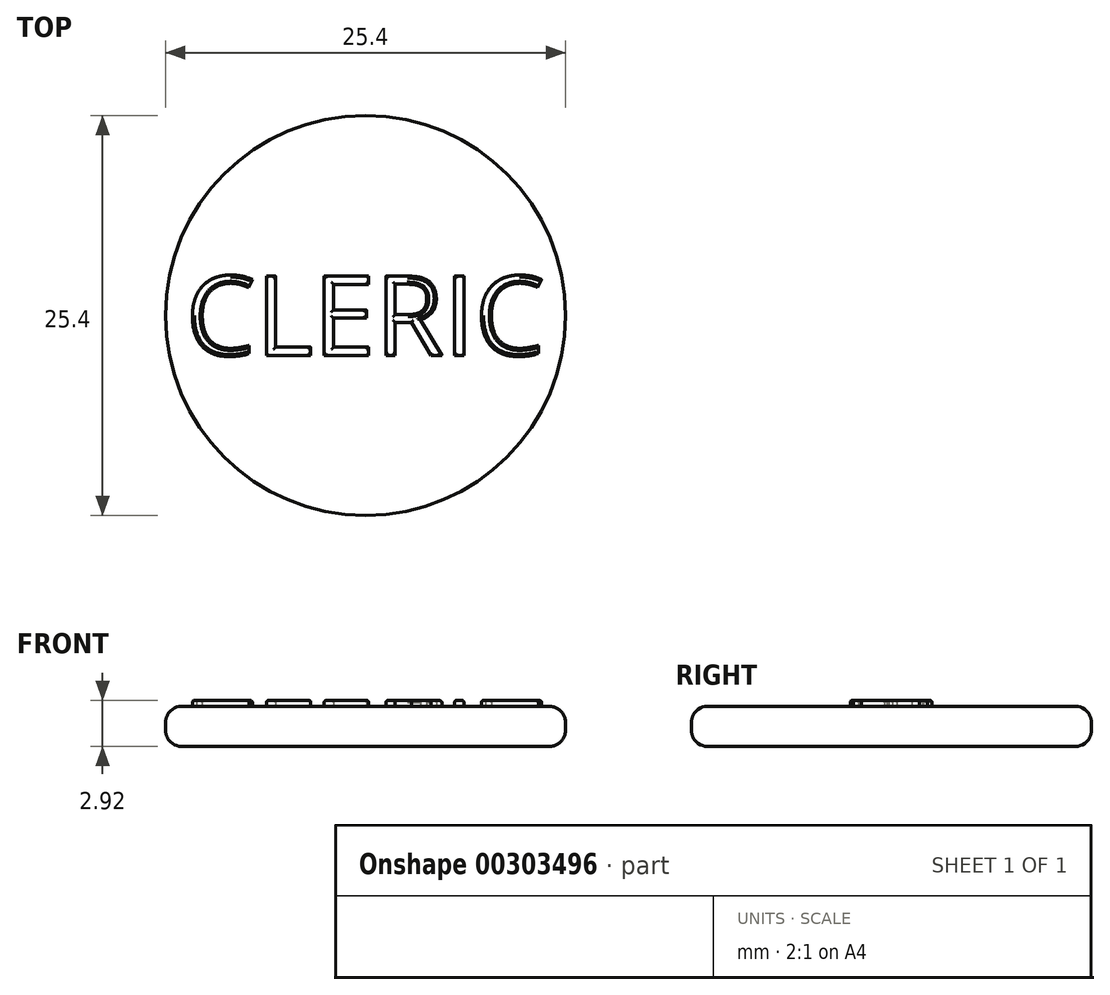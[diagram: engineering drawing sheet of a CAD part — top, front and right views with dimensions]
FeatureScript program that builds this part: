
annotation { "Feature Type Name" : "Feature", "Feature Type Description" : "" }
export const myFeature = defineFeature(function(context is Context, id is Id, definition is map)
    precondition{}
    {
        {
            var Q0;
            Q0=qCreatedBy(makeId("Top.planeOp"),FACE);
            var sketch = newSketch(context, id + "F0", { "sketchPlane" : qUnion([Q0])});
            skCircle(sketch, "E0", {"center": v(0, 0) * mm, "radius": 12.7 * mm});
            skLineSegment(sketch, "E1", {"start": v(0, 0) * mm, "end": v(-11.43, 0) * mm});
            skLineSegment(sketch, "E2", {"start": v(-11.43, 0) * mm, "end": v(-11.43, 2.54) * mm});
            skLineSegment(sketch, "E3", {"start": v(-11.43, 0) * mm, "end": v(-11.43, -2.54) * mm});
            skText(sketch, "E4", { "text": "CLERIC", "fontName": "OpenSans-Regular.ttf"});
            const initialGuessF0  = {"E4": [-0.01143, -0.00254, 1, 0, 0.00508]};
            skSetInitialGuess(sketch, initialGuessF0);
            skSolve(sketch);
        }
        {
            var Q0;
            Q0 = qSketchRegion(id + "F0", true);
            var Q1;
            Q1=makeQuery(id+"F0.imprint","IMPRINT",FACE,{"disambiguationData":[TD([[makeQuery(id+"F0.imprint","IMPRINT",EDGE,{"derivedFrom":sQuery(id+"F0.wireOp",EDGE,"E4.sketch_text.stroke-44")}),1.0]])]});
            extrude(context, id + "F1", {"entities" : qUnion([Q0, Q1]), "depth" : 2.54 * mm});
        }
        {
            var Q0;
            Q0=makeQuery(id+"F0.imprint","IMPRINT",FACE,{"disambiguationData":[TD([[makeQuery(id+"F0.imprint","IMPRINT",EDGE,{"derivedFrom":sQuery(id+"F0.wireOp",EDGE,"E4.sketch_text.stroke-55")}),-1.0]])]});
            var Q1;
            Q1=makeQuery(id+"F0.imprint","IMPRINT",FACE,{"disambiguationData":[TD([[makeQuery(id+"F0.imprint","IMPRINT",EDGE,{"derivedFrom":sQuery(id+"F0.wireOp",EDGE,"E4.sketch_text.stroke-51")}),-1.0]])]});
            var Q2;
            Q2=makeQuery(id+"F0.imprint","IMPRINT",FACE,{"disambiguationData":[TD([[makeQuery(id+"F0.imprint","IMPRINT",EDGE,{"derivedFrom":sQuery(id+"F0.wireOp",EDGE,"E4.sketch_text.stroke-33")}),-1.0]])]});
            var Q3;
            {var subQ0=sQuery(id+"F0.wireOp",EDGE,"E4.sketch_text.stroke-21");Q3=makeQuery(id+"F0.imprint","IMPRINT",FACE,{"disambiguationData":[TD([[makeQuery(id+"F0.imprint","IMPRINT",EDGE,{"derivedFrom":subQ0}),-1.0]])]});}
            var Q4;
            {var subQ0=sQuery(id+"F0.wireOp",EDGE,"E4.sketch_text.stroke-18");Q4=makeQuery(id+"F0.imprint","IMPRINT",FACE,{"disambiguationData":[TD([[makeQuery(id+"F0.imprint","IMPRINT",EDGE,{"derivedFrom":subQ0}),-1.0]])]});}
            var Q5;
            {var subQ5=sQuery(id+"F0.wireOp",EDGE,"E4.sketch_text.stroke-16");Q5=makeQuery(id+"F0.imprint","IMPRINT",FACE,{"disambiguationData":[TD([[makeQuery(id+"F0.imprint","IMPRINT",EDGE,{"derivedFrom":subQ5}),-1.0]])]});}
            var Q6;
            {var subQ0=sQuery(id+"F0.wireOp",EDGE,"E4.sketch_text.stroke-2");Q6=makeQuery(id+"F0.imprint","IMPRINT",FACE,{"disambiguationData":[TD([[makeQuery(id+"F0.imprint","IMPRINT",EDGE,{"derivedFrom":subQ0}),-1.0]])]});}
            var Q7;
            {var subQ4=sQuery(id+"F0.wireOp",EDGE,"E4.sketch_text.stroke-0");Q7=makeQuery(id+"F0.imprint","IMPRINT",FACE,{"disambiguationData":[TD([[makeQuery(id+"F0.imprint","IMPRINT",EDGE,{"derivedFrom":subQ4}),-1.0]])]});}
            extrude(context, id + "F2", {"entities" : qUnion([Q0, Q1, Q2, Q3, Q4, Q5, Q6, Q7]), "depth" : 2.92 * mm, "hasSecondDirection" : true, "secondDirectionOppositeDirection" : false, "secondDirectionDepth" : 0.64 * mm});
        }
        {
            var Q0;
            Q0=makeQuery(id+"F2.opExtrude","CAP_FACE",FACE,{"disambiguationData":[OSD([sQuery(id+"F0.wireOp",EDGE,"E4.sketch_text.stroke-0"),sQuery(id+"F0.wireOp",EDGE,"E4.sketch_text.stroke-1"),sQuery(id+"F0.wireOp",EDGE,"E4.sketch_text.stroke-2"),sQuery(id+"F0.wireOp",EDGE,"E4.sketch_text.stroke-3"),sQuery(id+"F0.wireOp",EDGE,"E4.sketch_text.stroke-4"),sQuery(id+"F0.wireOp",EDGE,"E4.sketch_text.stroke-5"),sQuery(id+"F0.wireOp",EDGE,"E4.sketch_text.stroke-6"),sQuery(id+"F0.wireOp",EDGE,"E4.sketch_text.stroke-7"),sQuery(id+"F0.wireOp",EDGE,"E4.sketch_text.stroke-8"),sQuery(id+"F0.wireOp",EDGE,"E4.sketch_text.stroke-9"),sQuery(id+"F0.wireOp",EDGE,"E4.sketch_text.stroke-10"),sQuery(id+"F0.wireOp",EDGE,"E4.sketch_text.stroke-11"),sQuery(id+"F0.wireOp",EDGE,"E4.sketch_text.stroke-12"),sQuery(id+"F0.wireOp",EDGE,"E4.sketch_text.stroke-13"),sQuery(id+"F0.wireOp",EDGE,"E4.sketch_text.stroke-14")])],"isStart":false});
            var Q1;
            Q1=makeQuery(id+"F2.opExtrude","CAP_FACE",FACE,{"disambiguationData":[OSD([sQuery(id+"F0.wireOp",EDGE,"E4.sketch_text.stroke-15"),sQuery(id+"F0.wireOp",EDGE,"E4.sketch_text.stroke-16"),sQuery(id+"F0.wireOp",EDGE,"E4.sketch_text.stroke-17"),sQuery(id+"F0.wireOp",EDGE,"E4.sketch_text.stroke-18"),sQuery(id+"F0.wireOp",EDGE,"E4.sketch_text.stroke-19"),sQuery(id+"F0.wireOp",EDGE,"E4.sketch_text.stroke-20")])],"isStart":false});
            var Q2;
            Q2=makeQuery(id+"F2.opExtrude","CAP_FACE",FACE,{"disambiguationData":[OSD([sQuery(id+"F0.wireOp",EDGE,"E4.sketch_text.stroke-21"),sQuery(id+"F0.wireOp",EDGE,"E4.sketch_text.stroke-22"),sQuery(id+"F0.wireOp",EDGE,"E4.sketch_text.stroke-23"),sQuery(id+"F0.wireOp",EDGE,"E4.sketch_text.stroke-24"),sQuery(id+"F0.wireOp",EDGE,"E4.sketch_text.stroke-25"),sQuery(id+"F0.wireOp",EDGE,"E4.sketch_text.stroke-26"),sQuery(id+"F0.wireOp",EDGE,"E4.sketch_text.stroke-27"),sQuery(id+"F0.wireOp",EDGE,"E4.sketch_text.stroke-28"),sQuery(id+"F0.wireOp",EDGE,"E4.sketch_text.stroke-29"),sQuery(id+"F0.wireOp",EDGE,"E4.sketch_text.stroke-30"),sQuery(id+"F0.wireOp",EDGE,"E4.sketch_text.stroke-31"),sQuery(id+"F0.wireOp",EDGE,"E4.sketch_text.stroke-32")])],"isStart":false});
            var Q3;
            Q3=makeQuery(id+"F2.opExtrude","CAP_FACE",FACE,{"disambiguationData":[OSD([sQuery(id+"F0.wireOp",EDGE,"E4.sketch_text.stroke-33"),sQuery(id+"F0.wireOp",EDGE,"E4.sketch_text.stroke-34"),sQuery(id+"F0.wireOp",EDGE,"E4.sketch_text.stroke-35"),sQuery(id+"F0.wireOp",EDGE,"E4.sketch_text.stroke-36"),sQuery(id+"F0.wireOp",EDGE,"E4.sketch_text.stroke-37"),sQuery(id+"F0.wireOp",EDGE,"E4.sketch_text.stroke-38"),sQuery(id+"F0.wireOp",EDGE,"E4.sketch_text.stroke-39"),sQuery(id+"F0.wireOp",EDGE,"E4.sketch_text.stroke-40"),sQuery(id+"F0.wireOp",EDGE,"E4.sketch_text.stroke-41"),sQuery(id+"F0.wireOp",EDGE,"E4.sketch_text.stroke-42"),sQuery(id+"F0.wireOp",EDGE,"E4.sketch_text.stroke-43"),sQuery(id+"F0.wireOp",EDGE,"E4.sketch_text.stroke-44"),sQuery(id+"F0.wireOp",EDGE,"E4.sketch_text.stroke-45"),sQuery(id+"F0.wireOp",EDGE,"E4.sketch_text.stroke-46"),sQuery(id+"F0.wireOp",EDGE,"E4.sketch_text.stroke-47"),sQuery(id+"F0.wireOp",EDGE,"E4.sketch_text.stroke-48"),sQuery(id+"F0.wireOp",EDGE,"E4.sketch_text.stroke-49"),sQuery(id+"F0.wireOp",EDGE,"E4.sketch_text.stroke-50")])],"isStart":false});
            var Q4;
            Q4=makeQuery(id+"F2.opExtrude","CAP_FACE",FACE,{"disambiguationData":[OSD([sQuery(id+"F0.wireOp",EDGE,"E4.sketch_text.stroke-51"),sQuery(id+"F0.wireOp",EDGE,"E4.sketch_text.stroke-52"),sQuery(id+"F0.wireOp",EDGE,"E4.sketch_text.stroke-53"),sQuery(id+"F0.wireOp",EDGE,"E4.sketch_text.stroke-54")])],"isStart":false});
            var Q5;
            Q5=makeQuery(id+"F2.opExtrude","CAP_FACE",FACE,{"disambiguationData":[OSD([sQuery(id+"F0.wireOp",EDGE,"E4.sketch_text.stroke-55"),sQuery(id+"F0.wireOp",EDGE,"E4.sketch_text.stroke-56"),sQuery(id+"F0.wireOp",EDGE,"E4.sketch_text.stroke-57"),sQuery(id+"F0.wireOp",EDGE,"E4.sketch_text.stroke-58"),sQuery(id+"F0.wireOp",EDGE,"E4.sketch_text.stroke-59"),sQuery(id+"F0.wireOp",EDGE,"E4.sketch_text.stroke-60"),sQuery(id+"F0.wireOp",EDGE,"E4.sketch_text.stroke-61"),sQuery(id+"F0.wireOp",EDGE,"E4.sketch_text.stroke-62"),sQuery(id+"F0.wireOp",EDGE,"E4.sketch_text.stroke-63"),sQuery(id+"F0.wireOp",EDGE,"E4.sketch_text.stroke-64"),sQuery(id+"F0.wireOp",EDGE,"E4.sketch_text.stroke-65"),sQuery(id+"F0.wireOp",EDGE,"E4.sketch_text.stroke-66"),sQuery(id+"F0.wireOp",EDGE,"E4.sketch_text.stroke-67"),sQuery(id+"F0.wireOp",EDGE,"E4.sketch_text.stroke-68"),sQuery(id+"F0.wireOp",EDGE,"E4.sketch_text.stroke-69")])],"isStart":false});
            fillet(context, id + "F3", {"entities" : qUnion([Q0, Q1, Q2, Q3, Q4, Q5]), "radius" : 0.13 * mm, "tangentPropagation" : true, "allowEdgeOverflow" : false});
        }
        {
            var Q0;
            Q0=makeQuery(id+"F1.opExtrude","CAP_EDGE",EDGE,{"disambiguationData":[OSD([sQuery(id+"F0.wireOp",EDGE,"E0")])],"isStart":false});
            var Q1;
            Q1=makeQuery(id+"F1.opExtrude","CAP_EDGE",EDGE,{"disambiguationData":[OSD([sQuery(id+"F0.wireOp",EDGE,"E0")])],"isStart":true});
            fillet(context, id + "F4", {"entities" : qUnion([Q0, Q1]), "radius" : 1.02 * mm, "tangentPropagation" : true, "allowEdgeOverflow" : false});
        }
        {
            var Q0;
            Q0=makeQuery(id+"F0.imprint","IMPRINT",FACE,{"disambiguationData":[TD([[makeQuery(id+"F0.imprint","IMPRINT",EDGE,{"derivedFrom":sQuery(id+"F0.wireOp",EDGE,"E4.sketch_text.stroke-55")}),-1.0]])]});
            var Q1;
            Q1=makeQuery(id+"F0.imprint","IMPRINT",FACE,{"disambiguationData":[TD([[makeQuery(id+"F0.imprint","IMPRINT",EDGE,{"derivedFrom":sQuery(id+"F0.wireOp",EDGE,"E4.sketch_text.stroke-51")}),-1.0]])]});
            var Q2;
            Q2=makeQuery(id+"F0.imprint","IMPRINT",FACE,{"disambiguationData":[TD([[makeQuery(id+"F0.imprint","IMPRINT",EDGE,{"derivedFrom":sQuery(id+"F0.wireOp",EDGE,"E4.sketch_text.stroke-33")}),-1.0]])]});
            var Q3;
            {var subQ0=sQuery(id+"F0.wireOp",EDGE,"E4.sketch_text.stroke-21");Q3=makeQuery(id+"F0.imprint","IMPRINT",FACE,{"disambiguationData":[TD([[makeQuery(id+"F0.imprint","IMPRINT",EDGE,{"derivedFrom":subQ0}),-1.0]])]});}
            var Q4;
            {var subQ5=sQuery(id+"F0.wireOp",EDGE,"E4.sketch_text.stroke-16");Q4=makeQuery(id+"F0.imprint","IMPRINT",FACE,{"disambiguationData":[TD([[makeQuery(id+"F0.imprint","IMPRINT",EDGE,{"derivedFrom":subQ5}),-1.0]])]});}
            var Q5;
            {var subQ0=sQuery(id+"F0.wireOp",EDGE,"E4.sketch_text.stroke-18");Q5=makeQuery(id+"F0.imprint","IMPRINT",FACE,{"disambiguationData":[TD([[makeQuery(id+"F0.imprint","IMPRINT",EDGE,{"derivedFrom":subQ0}),-1.0]])]});}
            var Q6;
            {var subQ4=sQuery(id+"F0.wireOp",EDGE,"E4.sketch_text.stroke-0");Q6=makeQuery(id+"F0.imprint","IMPRINT",FACE,{"disambiguationData":[TD([[makeQuery(id+"F0.imprint","IMPRINT",EDGE,{"derivedFrom":subQ4}),-1.0]])]});}
            var Q7;
            {var subQ0=sQuery(id+"F0.wireOp",EDGE,"E4.sketch_text.stroke-2");Q7=makeQuery(id+"F0.imprint","IMPRINT",FACE,{"disambiguationData":[TD([[makeQuery(id+"F0.imprint","IMPRINT",EDGE,{"derivedFrom":subQ0}),-1.0]])]});}
            extrude(context, id + "F5", {"entities" : qUnion([Q0, Q1, Q2, Q3, Q4, Q5, Q6, Q7]), "operationType" : NewBodyOperationType.ADD, "depth" : 0.64 * mm});
        }
    });
